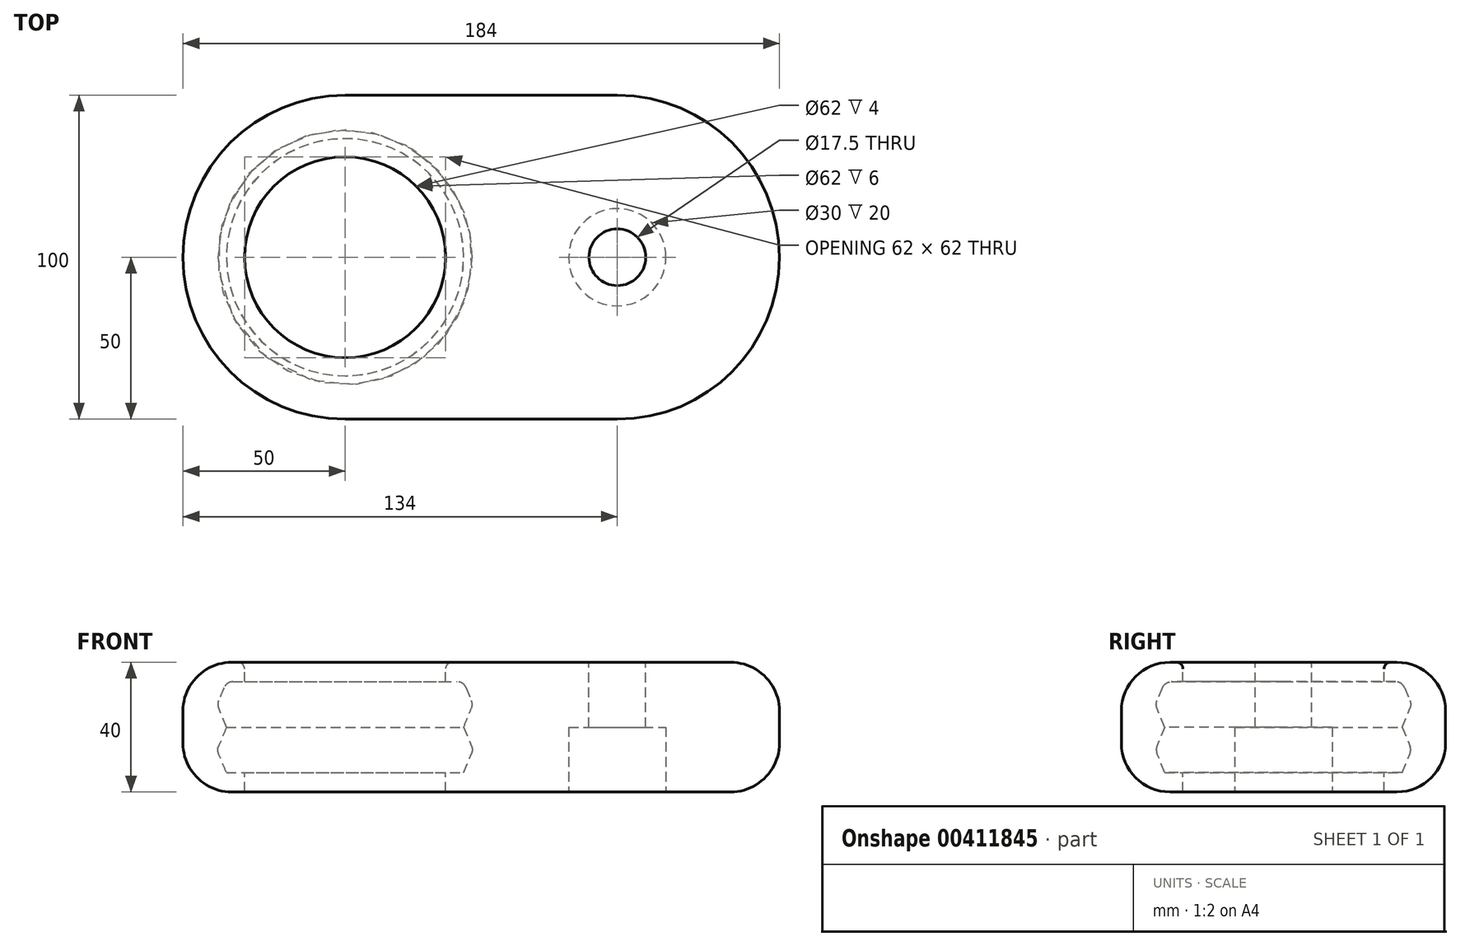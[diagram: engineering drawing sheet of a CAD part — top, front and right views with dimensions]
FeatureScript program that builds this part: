
annotation { "Feature Type Name" : "Feature", "Feature Type Description" : "" }
export const myFeature = defineFeature(function(context is Context, id is Id, definition is map)
    precondition{}
    {
        {
            var Q0;
            Q0=qCreatedBy(makeId("Top.planeOp"),FACE);
            var sketch = newSketch(context, id + "F0", { "sketchPlane" : qUnion([Q0])});
            skArc(sketch, "E0", {"start": v(0, 50) * mm, "mid": v(-50, 0) * mm, "end": v(0, -50) * mm});
            skArc(sketch, "E1", {"start": v(84, -50) * mm, "mid": v(134, 0) * mm, "end": v(84, 50) * mm});
            skLineSegment(sketch, "E2", {"start": v(0, -50) * mm, "end": v(84, -50) * mm});
            skLineSegment(sketch, "E3", {"start": v(0, 50) * mm, "end": v(84, 50) * mm});
            skCircle(sketch, "E4", {"center": v(84, 0) * mm, "radius": 8.75 * mm});
            skCircle(sketch, "E5", {"center": v(0, 0) * mm, "radius": 31 * mm});
            skSolve(sketch);
        }
        {
            var Q0;
            Q0=qCreatedBy(makeId("Front.planeOp"),FACE);
            var sketch = newSketch(context, id + "F1", { "sketchPlane" : qUnion([Q0])});
            skLineSegment(sketch, "E6.MirrorCS", {"start": v(-31, 0) * mm, "end": v(-31, -6) * mm});
            skLineSegment(sketch, "E7.MirrorCS", {"start": v(-31, -6) * mm, "end": v(-36.6, -6) * mm});
            skLineSegment(sketch, "E8.MirrorCS", {"start": v(-39.5, -13) * mm, "end": v(-36.6, -6) * mm});
            skLineSegment(sketch, "E9.MirrorCS", {"start": v(-39.5, -13) * mm, "end": v(-36.6, -20) * mm});
            skLineSegment(sketch, "E10.MirrorCS", {"start": v(-39.5, -27) * mm, "end": v(-36.6, -20) * mm});
            skLineSegment(sketch, "E11.MirrorCS", {"start": v(-39.5, -27) * mm, "end": v(-36.6, -34) * mm});
            skLineSegment(sketch, "E12.MirrorCS", {"start": v(-31, -34) * mm, "end": v(-36.58, -34) * mm});
            skLineSegment(sketch, "E13", {"start": v(-31, -40) * mm, "end": v(0, -40) * mm});
            skPoint(sketch, "E14.start.orphan", {"position": v(31, 0) * mm});
            skPoint(sketch, "E15.start.orphan", {"position": v(31, -6) * mm});
            skPoint(sketch, "E16.end.orphan", {"position": v(36.6, -6) * mm});
            skPoint(sketch, "E17.MirrorCS.end.orphan", {"position": v(36.6, -20) * mm});
            skPoint(sketch, "E17.MirrorCS.start.orphan", {"position": v(39.5, -13) * mm});
            skLineSegment(sketch, "E18", {"start": v(0, 0) * mm, "end": v(0, -40) * mm});
            skLineSegment(sketch, "E19", {"start": v(-31, -34) * mm, "end": v(-31, -40) * mm});
            skPoint(sketch, "E20.MirrorCS.end.orphan", {"position": v(0, 0) * mm});
            skPoint(sketch, "E21.MirrorCS.start.orphan", {"position": v(39.5, -27) * mm});
            skPoint(sketch, "E22.MirrorCS.end.orphan", {"position": v(36.58, -34) * mm});
            skPoint(sketch, "E22.MirrorCS.start.orphan", {"position": v(31, -34) * mm});
            skPoint(sketch, "E23.MirrorCS.end.orphan", {"position": v(0, -40) * mm});
            skPoint(sketch, "E23.MirrorCS.start.orphan", {"position": v(31, -40) * mm});
            skPoint(sketch, "E24.MirrorCS.end.orphan", {"position": v(36.6, -34) * mm});
            skLineSegment(sketch, "E25", {"start": v(-31, 0) * mm, "end": v(0, 0) * mm});
            skLineSegment(sketch, "E26", {"start": v(0, -40) * mm, "end": v(0, 0) * mm});
            skLineSegment(sketch, "E27", {"start": v(0, -40) * mm, "end": v(-31, -40) * mm});
            skLineSegment(sketch, "E28", {"start": v(-31, -40) * mm, "end": v(-31, -34) * mm});
            skLineSegment(sketch, "E29", {"start": v(-36.58, -34) * mm, "end": v(-39.5, -27) * mm});
            skLineSegment(sketch, "E30", {"start": v(-36.6, -20) * mm, "end": v(-39.5, -13) * mm});
            skLineSegment(sketch, "E31", {"start": v(-36.6, -6) * mm, "end": v(-31, -6) * mm});
            skSolve(sketch);
        }
        {
            var Q0;
            Q0=makeQuery(id+"F0.imprint","IMPRINT",FACE,{"disambiguationData":[TD([[makeQuery(id+"F0.imprint","IMPRINT",EDGE,{"derivedFrom":sQuery(id+"F0.wireOp",EDGE,"E0")}),1.0]])]});
            extrude(context, id + "F2", {"entities" : qUnion([Q0]), "oppositeDirection" : true, "depth" : 40 * mm});
        }
        {
            var Q0;
            Q0=makeQuery(id+"F2.opExtrude","CAP_FACE",FACE,{"disambiguationData":[OSD([sQuery(id+"F0.wireOp",EDGE,"E0"),sQuery(id+"F0.wireOp",EDGE,"E1"),sQuery(id+"F0.wireOp",EDGE,"E2"),sQuery(id+"F0.wireOp",EDGE,"E3"),sQuery(id+"F0.wireOp",EDGE,"E4")])],"isStart":false});
            var sketch = newSketch(context, id + "F3", { "sketchPlane" : qUnion([Q0])});
            skCircle(sketch, "E32", {"center": v(84, 0) * mm, "radius": 15 * mm});
            skSolve(sketch);
        }
        {
            var Q0;
            Q0=sQuery(id+"F3.wireOp",VERTEX,"E32.center");
            var Q1;
            Q1=makeQuery(id+"F2.opExtrude","SWEPT_BODY",BODY,{"disambiguationData":[OSD([sQuery(id+"F0.wireOp",EDGE,"E0"),sQuery(id+"F0.wireOp",EDGE,"E1"),sQuery(id+"F0.wireOp",EDGE,"E2"),sQuery(id+"F0.wireOp",EDGE,"E3"),sQuery(id+"F0.wireOp",EDGE,"E4")])]});
            hole(context, id + "F4", {"style" : HoleStyle.C_BORE, "endStyle" : HoleEndStyle.BLIND, "holeDiameter" : 17.5 * mm, "cBoreDiameter" : 30 * mm, "cBoreDepth" : 20 * mm, "holeDepth" : 50 * mm, "tappedDepth" : 12 * mm, "tapClearance" : 3, "locations" : qUnion([Q0]), "scope" : qUnion([Q1])});
        }
        {
            var Q0;
            Q0=makeQuery(id+"F1.imprint","IMPRINT",FACE,{"disambiguationData":[TD([[makeQuery(id+"F1.imprint","IMPRINT",EDGE,{"derivedFrom":sQuery(id+"F1.wireOp",EDGE,"E6.MirrorCS")}),1.0]])]});
            var Q1;
            Q1=sQuery(id+"F1.wireOp",EDGE,"E26");
            revolve(context, id + "F5", {"entities" : qUnion([Q0]), "axis" : qUnion([Q1]), "revolveType" : RevolveType.FULL});
        }
        {
            var Q0;
            Q0=makeQuery(id+"F5.opRevolve","SWEPT_EDGE",EDGE,{"disambiguationData":[OSD([sQuery(id+"F1.wireOp",EDGE,"E10.MirrorCS"),sQuery(id+"F1.wireOp",EDGE,"E29")])]});
            var Q1;
            Q1=makeQuery(id+"F5.opRevolve","SWEPT_EDGE",EDGE,{"disambiguationData":[OSD([sQuery(id+"F1.wireOp",EDGE,"E8.MirrorCS"),sQuery(id+"F1.wireOp",EDGE,"E30")])]});
            fillet(context, id + "F6", {"entities" : qUnion([Q0, Q1]), "radius" : 3 * mm, "allowEdgeOverflow" : false});
        }
        {
            var Q0;
            Q0=makeQuery(id+"F5.opRevolve","SWEPT_BODY",BODY,{"disambiguationData":[OSD([sQuery(id+"F1.wireOp",EDGE,"E6.MirrorCS"),sQuery(id+"F1.wireOp",EDGE,"E8.MirrorCS"),sQuery(id+"F1.wireOp",EDGE,"E10.MirrorCS"),sQuery(id+"F1.wireOp",EDGE,"E12.MirrorCS"),sQuery(id+"F1.wireOp",EDGE,"E25"),sQuery(id+"F1.wireOp",EDGE,"E26"),sQuery(id+"F1.wireOp",EDGE,"E27"),sQuery(id+"F1.wireOp",EDGE,"E28"),sQuery(id+"F1.wireOp",EDGE,"E29"),sQuery(id+"F1.wireOp",EDGE,"E30"),sQuery(id+"F1.wireOp",EDGE,"E31")])]});
            var Q1;
            Q1=makeQuery(id+"F2.opExtrude","SWEPT_BODY",BODY,{"disambiguationData":[OSD([sQuery(id+"F0.wireOp",EDGE,"E0"),sQuery(id+"F0.wireOp",EDGE,"E1"),sQuery(id+"F0.wireOp",EDGE,"E2"),sQuery(id+"F0.wireOp",EDGE,"E3"),sQuery(id+"F0.wireOp",EDGE,"E4"),sQuery(id+"F0.wireOp",EDGE,"E5")])]});
            booleanBodies(context, id + "F7", {"operationType" : BooleanOperationType.SUBTRACTION, "tools" : qUnion([Q0]), "targets" : qUnion([Q1])});
        }
        {
            var Q0;
            Q0=makeQuery(id+"F2.opExtrude","CAP_EDGE",EDGE,{"disambiguationData":[OSD([sQuery(id+"F0.wireOp",EDGE,"E2")])],"isStart":true});
            var Q1;
            Q1=makeQuery(id+"F2.opExtrude","CAP_EDGE",EDGE,{"disambiguationData":[OSD([sQuery(id+"F0.wireOp",EDGE,"E2")])],"isStart":false});
            fillet(context, id + "F8", {"entities" : qUnion([Q0, Q1]), "radius" : 15 * mm, "tangentPropagation" : true, "allowEdgeOverflow" : false});
        }
        {
            var Q0;
            Q0=makeQuery(id+"F2.opExtrude","CAP_EDGE",EDGE,{"disambiguationData":[OSD([sQuery(id+"F0.wireOp",EDGE,"E5")])],"isStart":true});
            fillet(context, id + "F9", {"entities" : qUnion([Q0]), "radius" : 2 * mm, "tangentPropagation" : true, "allowEdgeOverflow" : false});
        }
    });
